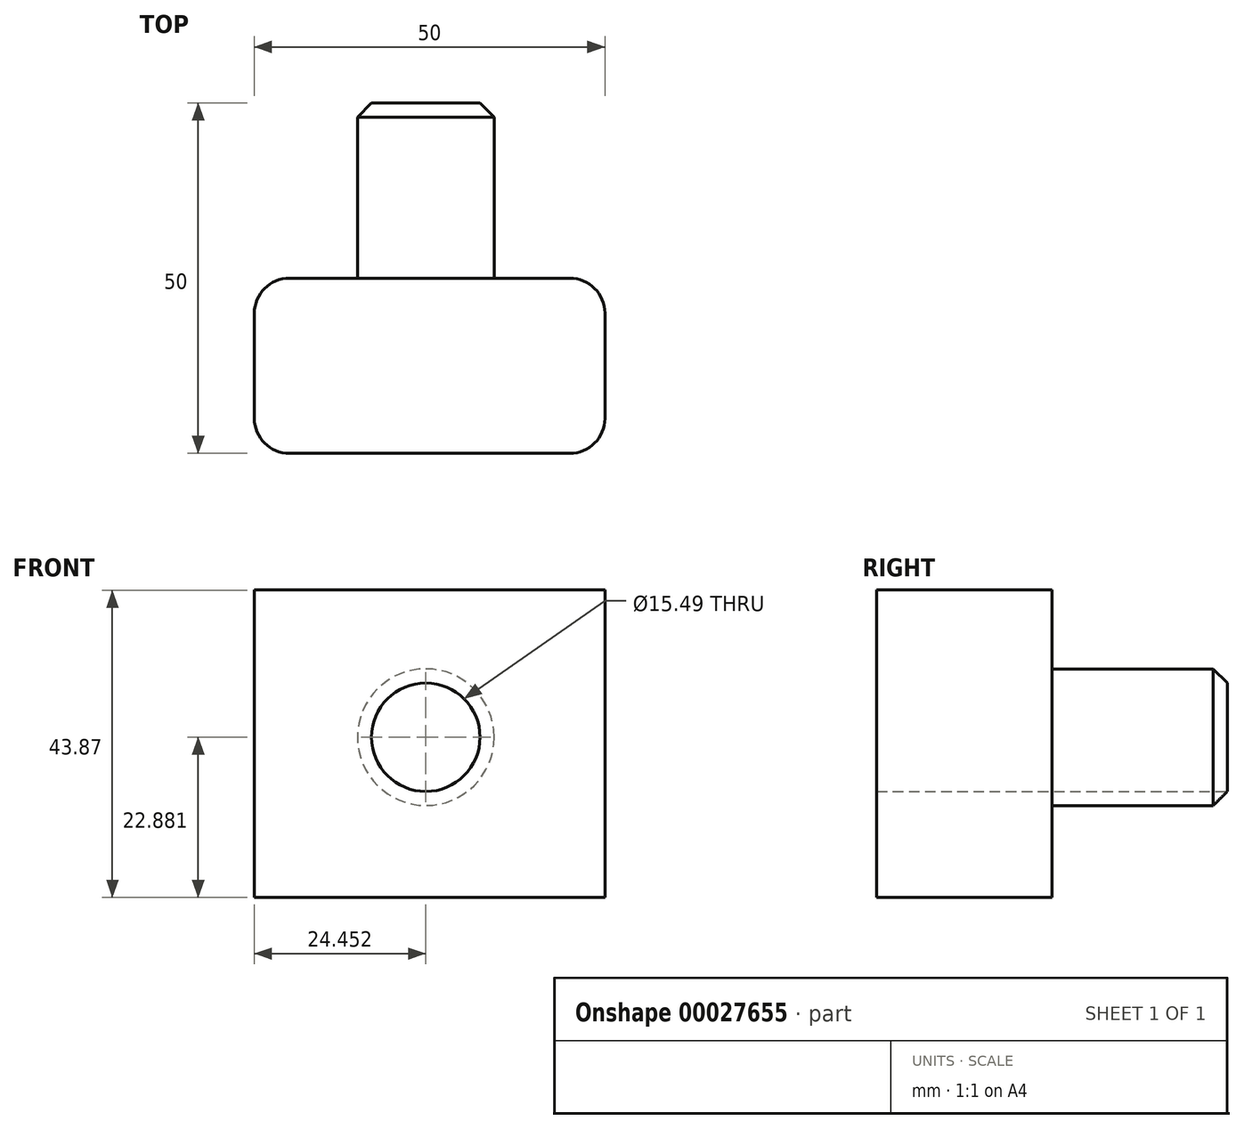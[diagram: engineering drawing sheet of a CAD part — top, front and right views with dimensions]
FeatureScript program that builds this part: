
annotation { "Feature Type Name" : "Feature", "Feature Type Description" : "" }
export const myFeature = defineFeature(function(context is Context, id is Id, definition is map)
    precondition{}
    {
        {
            var Q0;
            Q0=qCreatedBy(makeId("Front.planeOp"),FACE);
            var sketch = newSketch(context, id + "F0", { "sketchPlane" : qUnion([Q0])});
            skLineSegment(sketch, "E0.bottom", {"start": v(0, 0) * mm, "end": v(-50, 0) * mm});
            skLineSegment(sketch, "E0.top", {"start": v(0, 43.87) * mm, "end": v(-50, 43.87) * mm});
            skLineSegment(sketch, "E0.left", {"start": v(0, 0) * mm, "end": v(0, 43.87) * mm});
            skLineSegment(sketch, "E0.right", {"start": v(-50, 0) * mm, "end": v(-50, 43.87) * mm});
            skSolve(sketch);
        }
        {
            var Q0;
            Q0=makeQuery(id+"F0.imprint","IMPRINT",FACE,{"disambiguationData":[TD([[makeQuery(id+"F0.imprint","IMPRINT",EDGE,{"derivedFrom":sQuery(id+"F0.wireOp",EDGE,"E0.bottom")}),-1.0]])]});
            extrude(context, id + "F1", {"entities" : qUnion([Q0]), "depth" : 25 * mm});
        }
        {
            var Q0;
            Q0=makeQuery(id+"F1.opExtrude","CAP_FACE",FACE,{"disambiguationData":[OSD([sQuery(id+"F0.wireOp",EDGE,"E0.bottom"),sQuery(id+"F0.wireOp",EDGE,"E0.top"),sQuery(id+"F0.wireOp",EDGE,"E0.left"),sQuery(id+"F0.wireOp",EDGE,"E0.right")])],"isStart":false});
            var sketch = newSketch(context, id + "F2", { "sketchPlane" : qUnion([Q0])});
            skCircle(sketch, "E1", {"center": v(-25.55, 22.88) * mm, "radius": 9.75 * mm});
            skSolve(sketch);
        }
        {
            var Q0;
            Q0=makeQuery(id+"F2.imprint","IMPRINT",FACE,{"disambiguationData":[TD([[makeQuery(id+"F2.imprint","IMPRINT",EDGE,{"derivedFrom":sQuery(id+"F2.wireOp",EDGE,"E1")}),1.0]])]});
            extrude(context, id + "F3", {"entities" : qUnion([Q0]), "operationType" : NewBodyOperationType.ADD, "oppositeDirection" : true, "depth" : 50 * mm});
        }
        {
            var Q0;
            Q0=makeQuery(id+"F1.opExtrude","CAP_EDGE",EDGE,{"disambiguationData":[OSD([sQuery(id+"F0.wireOp",EDGE,"E0.left")])],"isStart":false});
            var Q1;
            Q1=makeQuery(id+"F1.opExtrude","CAP_EDGE",EDGE,{"disambiguationData":[OSD([sQuery(id+"F0.wireOp",EDGE,"E0.right")])],"isStart":false});
            var Q2;
            Q2=makeQuery(id+"F1.opExtrude","CAP_EDGE",EDGE,{"disambiguationData":[OSD([sQuery(id+"F0.wireOp",EDGE,"E0.left")])],"isStart":true});
            var Q3;
            Q3=makeQuery(id+"F1.opExtrude","CAP_EDGE",EDGE,{"disambiguationData":[OSD([sQuery(id+"F0.wireOp",EDGE,"E0.right")])],"isStart":true});
            fillet(context, id + "F4", {"entities" : qUnion([Q0, Q1, Q2, Q3]), "radius" : 5 * mm, "tangentPropagation" : true, "allowEdgeOverflow" : false});
        }
        {
            var Q0;
            Q0=makeQuery(id+"F3.opExtrude","CAP_EDGE",EDGE,{"disambiguationData":[OSD([sQuery(id+"F2.wireOp",EDGE,"E1")])],"isStart":false});
            chamfer(context, id + "F5", {"entities" : qUnion([Q0]), "width" : 2 * mm, "tangentPropagation" : true});
        }
        {
            var Q0;
            Q0=makeQuery(id+"F3.opExtrude","CAP_FACE",FACE,{"disambiguationData":[OSD([sQuery(id+"F2.wireOp",EDGE,"E1")])],"isStart":false});
            extrude(context, id + "F6", {"entities" : qUnion([Q0]), "operationType" : NewBodyOperationType.REMOVE, "endBound" : BoundingType.UP_TO_NEXT, "oppositeDirection" : true, "depth" : 25 * mm});
        }
    });
